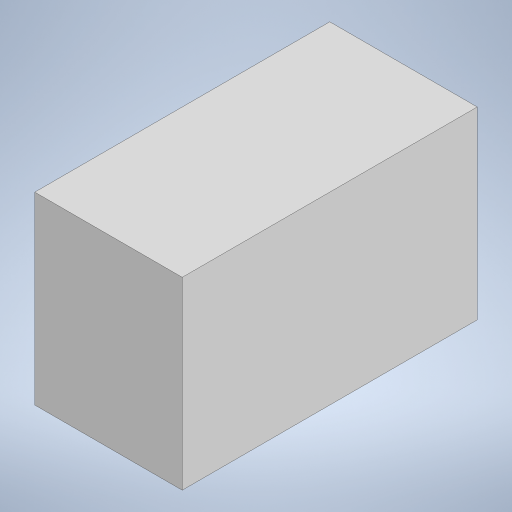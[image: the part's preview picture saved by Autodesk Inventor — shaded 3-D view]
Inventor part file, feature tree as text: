
AUTODESK INVENTOR PART (.ipt)
format: ipt  version: 2024 (Build 280153000, 153)  size: 204,800 bytes
history: native  units: mm
features: extrude x4, sketch x1, projected_geometry x1
ambient origin geometry x8: Origin, YZ Plane, XZ Plane, XY Plane, X Axis, Y Axis, Z Axis, Center Point
bodies: Body1 (feature_tree)
feature tree (6):
  sketch  "스케치1"
  extrude  "돌출3"  Depth=3.2mm
  extrude  "돌출4"  Depth=4.8mm
  extrude  "돌출5"  Depth=4.8mm
  extrude  "돌출6"  Depth=3.2mm
  projected_geometry  "투영된 루프1"
